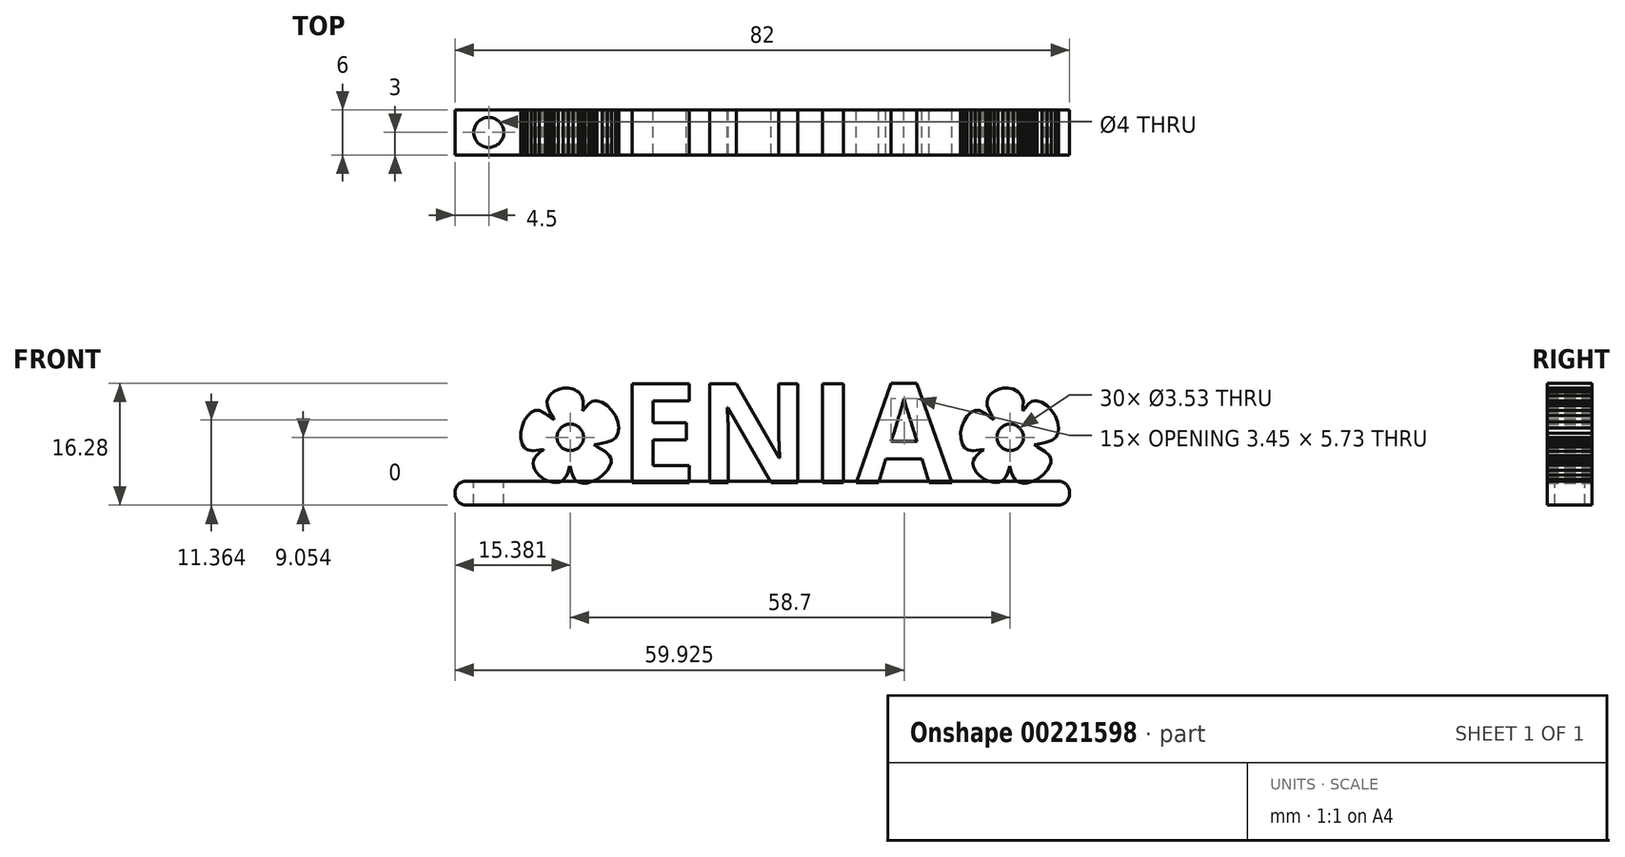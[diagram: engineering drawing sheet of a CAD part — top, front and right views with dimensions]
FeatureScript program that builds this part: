
annotation { "Feature Type Name" : "Feature", "Feature Type Description" : "" }
export const myFeature = defineFeature(function(context is Context, id is Id, definition is map)
    precondition{}
    {
        {
            var Q0;
            Q0=qCreatedBy(makeId("Front.planeOp"),FACE);
            var sketch = newSketch(context, id + "F0", { "sketchPlane" : qUnion([Q0])});
            skText(sketch, "E0", { "text": "   ENIA", "fontName": "OpenSans-Bold.ttf"});
            skLineSegment(sketch, "E1.0.0", {"start": v(-9.3, 0.1) * mm, "end": v(-8.53, 0.46) * mm});
            skLineSegment(sketch, "E1.0.1", {"start": v(-8.53, 0.46) * mm, "end": v(-7.79, 1.02) * mm});
            skLineSegment(sketch, "E1.0.2", {"start": v(-7.79, 1.02) * mm, "end": v(-7.18, 1.67) * mm});
            skLineSegment(sketch, "E1.0.3", {"start": v(-7.18, 1.67) * mm, "end": v(-6.78, 2.35) * mm});
            skLineSegment(sketch, "E1.0.4", {"start": v(-6.78, 2.35) * mm, "end": v(-6.68, 2.7) * mm});
            skLineSegment(sketch, "E1.0.5", {"start": v(-6.68, 2.7) * mm, "end": v(-6.67, 3.02) * mm});
            skLineSegment(sketch, "E1.0.6", {"start": v(-6.67, 3.02) * mm, "end": v(-6.73, 3.33) * mm});
            skLineSegment(sketch, "E1.0.7", {"start": v(-6.73, 3.33) * mm, "end": v(-6.89, 3.62) * mm});
            skLineSegment(sketch, "E1.0.8", {"start": v(-6.89, 3.62) * mm, "end": v(-7.48, 4.2) * mm});
            skLineSegment(sketch, "E1.0.9", {"start": v(-7.48, 4.2) * mm, "end": v(-8.5, 4.79) * mm});
            skLineSegment(sketch, "E1.0.10", {"start": v(-8.5, 4.79) * mm, "end": v(-8.93, 5.06) * mm});
            skLineSegment(sketch, "E1.0.11", {"start": v(-8.93, 5.06) * mm, "end": v(-8.42, 5.16) * mm});
            skLineSegment(sketch, "E1.0.12", {"start": v(-8.42, 5.16) * mm, "end": v(-7.31, 5.37) * mm});
            skLineSegment(sketch, "E1.0.13", {"start": v(-7.31, 5.37) * mm, "end": v(-6.55, 5.65) * mm});
            skLineSegment(sketch, "E1.0.14", {"start": v(-6.55, 5.65) * mm, "end": v(-6.05, 6.04) * mm});
            skLineSegment(sketch, "E1.0.15", {"start": v(-6.05, 6.04) * mm, "end": v(-5.76, 6.58) * mm});
            skLineSegment(sketch, "E1.0.16", {"start": v(-5.76, 6.58) * mm, "end": v(-5.64, 7.33) * mm});
            skLineSegment(sketch, "E1.0.17", {"start": v(-5.64, 7.33) * mm, "end": v(-5.78, 8.14) * mm});
            skLineSegment(sketch, "E1.0.18", {"start": v(-5.78, 8.14) * mm, "end": v(-6.1, 8.93) * mm});
            skLineSegment(sketch, "E1.0.19", {"start": v(-6.1, 8.93) * mm, "end": v(-6.6, 9.67) * mm});
            skLineSegment(sketch, "E1.0.20", {"start": v(-6.6, 9.67) * mm, "end": v(-7.2, 10.28) * mm});
            skLineSegment(sketch, "E1.0.21", {"start": v(-7.2, 10.28) * mm, "end": v(-7.86, 10.72) * mm});
            skLineSegment(sketch, "E1.0.22", {"start": v(-7.86, 10.72) * mm, "end": v(-8.55, 10.93) * mm});
            skLineSegment(sketch, "E1.0.23", {"start": v(-8.55, 10.93) * mm, "end": v(-8.88, 10.93) * mm});
            skLineSegment(sketch, "E1.0.24", {"start": v(-8.88, 10.93) * mm, "end": v(-9.2, 10.85) * mm});
            skLineSegment(sketch, "E1.0.25", {"start": v(-9.2, 10.85) * mm, "end": v(-9.65, 10.56) * mm});
            skLineSegment(sketch, "E1.0.26", {"start": v(-9.65, 10.56) * mm, "end": v(-10.14, 9.98) * mm});
            skLineSegment(sketch, "E1.0.27", {"start": v(-10.14, 9.98) * mm, "end": v(-10.45, 9.58) * mm});
            skLineSegment(sketch, "E1.0.28", {"start": v(-10.45, 9.58) * mm, "end": v(-10.4, 10.03) * mm});
            skLineSegment(sketch, "E1.0.29", {"start": v(-10.4, 10.03) * mm, "end": v(-10.4, 10.93) * mm});
            skLineSegment(sketch, "E1.0.30", {"start": v(-10.4, 10.93) * mm, "end": v(-10.6, 11.63) * mm});
            skLineSegment(sketch, "E1.0.31", {"start": v(-10.6, 11.63) * mm, "end": v(-11.04, 12.15) * mm});
            skLineSegment(sketch, "E1.0.32", {"start": v(-11.04, 12.15) * mm, "end": v(-11.71, 12.5) * mm});
            skLineSegment(sketch, "E1.0.33", {"start": v(-11.71, 12.5) * mm, "end": v(-12.4, 12.64) * mm});
            skLineSegment(sketch, "E1.0.34", {"start": v(-12.4, 12.64) * mm, "end": v(-13.07, 12.62) * mm});
            skLineSegment(sketch, "E1.0.35", {"start": v(-13.07, 12.62) * mm, "end": v(-13.7, 12.47) * mm});
            skLineSegment(sketch, "E1.0.36", {"start": v(-13.7, 12.47) * mm, "end": v(-14.26, 12.2) * mm});
            skLineSegment(sketch, "E1.0.37", {"start": v(-14.26, 12.2) * mm, "end": v(-14.72, 11.83) * mm});
            skLineSegment(sketch, "E1.0.38", {"start": v(-14.72, 11.83) * mm, "end": v(-15.05, 11.38) * mm});
            skLineSegment(sketch, "E1.0.39", {"start": v(-15.05, 11.38) * mm, "end": v(-15.22, 10.87) * mm});
            skLineSegment(sketch, "E1.0.40", {"start": v(-15.22, 10.87) * mm, "end": v(-15.2, 10.3) * mm});
            skLineSegment(sketch, "E1.0.41", {"start": v(-15.2, 10.3) * mm, "end": v(-14.83, 9.4) * mm});
            skLineSegment(sketch, "E1.0.42", {"start": v(-14.83, 9.4) * mm, "end": v(-14.35, 8.55) * mm});
            skLineSegment(sketch, "E1.0.43", {"start": v(-14.35, 8.55) * mm, "end": v(-14.3, 8.4) * mm});
            skLineSegment(sketch, "E1.0.44", {"start": v(-14.3, 8.4) * mm, "end": v(-14.48, 8.53) * mm});
            skLineSegment(sketch, "E1.0.45", {"start": v(-14.48, 8.53) * mm, "end": v(-15.4, 9.23) * mm});
            skLineSegment(sketch, "E1.0.46", {"start": v(-15.4, 9.23) * mm, "end": v(-16.22, 9.63) * mm});
            skLineSegment(sketch, "E1.0.47", {"start": v(-16.22, 9.63) * mm, "end": v(-16.8, 9.63) * mm});
            skLineSegment(sketch, "E1.0.48", {"start": v(-16.8, 9.63) * mm, "end": v(-17.36, 9.37) * mm});
            skLineSegment(sketch, "E1.0.49", {"start": v(-17.36, 9.37) * mm, "end": v(-17.85, 8.9) * mm});
            skLineSegment(sketch, "E1.0.50", {"start": v(-17.85, 8.9) * mm, "end": v(-18.26, 8.26) * mm});
            skLineSegment(sketch, "E1.0.51", {"start": v(-18.26, 8.26) * mm, "end": v(-18.56, 7.51) * mm});
            skLineSegment(sketch, "E1.0.52", {"start": v(-18.56, 7.51) * mm, "end": v(-18.72, 6.71) * mm});
            skLineSegment(sketch, "E1.0.53", {"start": v(-18.72, 6.71) * mm, "end": v(-18.72, 5.9) * mm});
            skLineSegment(sketch, "E1.0.54", {"start": v(-18.72, 5.9) * mm, "end": v(-18.52, 5.16) * mm});
            skLineSegment(sketch, "E1.0.55", {"start": v(-18.52, 5.16) * mm, "end": v(-18.2, 4.64) * mm});
            skLineSegment(sketch, "E1.0.56", {"start": v(-18.2, 4.64) * mm, "end": v(-17.75, 4.36) * mm});
            skLineSegment(sketch, "E1.0.57", {"start": v(-17.75, 4.36) * mm, "end": v(-17.1, 4.27) * mm});
            skLineSegment(sketch, "E1.0.58", {"start": v(-17.1, 4.27) * mm, "end": v(-16.21, 4.37) * mm});
            skLineSegment(sketch, "E1.0.59", {"start": v(-16.21, 4.37) * mm, "end": v(-15.7, 4.43) * mm});
            skLineSegment(sketch, "E1.0.60", {"start": v(-15.7, 4.43) * mm, "end": v(-15.67, 4.4) * mm});
            skLineSegment(sketch, "E1.0.61", {"start": v(-15.67, 4.4) * mm, "end": v(-15.78, 4.33) * mm});
            skLineSegment(sketch, "E1.0.62", {"start": v(-15.78, 4.33) * mm, "end": v(-16.17, 4.07) * mm});
            skLineSegment(sketch, "E1.0.63", {"start": v(-16.17, 4.07) * mm, "end": v(-16.55, 3.71) * mm});
            skLineSegment(sketch, "E1.0.64", {"start": v(-16.55, 3.71) * mm, "end": v(-16.87, 3.33) * mm});
            skLineSegment(sketch, "E1.0.65", {"start": v(-16.87, 3.33) * mm, "end": v(-17.04, 3) * mm});
            skLineSegment(sketch, "E1.0.66", {"start": v(-17.04, 3) * mm, "end": v(-17.08, 2.6) * mm});
            skLineSegment(sketch, "E1.0.67", {"start": v(-17.08, 2.6) * mm, "end": v(-17.02, 2.2) * mm});
            skLineSegment(sketch, "E1.0.68", {"start": v(-17.02, 2.2) * mm, "end": v(-16.87, 1.78) * mm});
            skLineSegment(sketch, "E1.0.69", {"start": v(-16.87, 1.78) * mm, "end": v(-16.62, 1.39) * mm});
            skLineSegment(sketch, "E1.0.70", {"start": v(-16.62, 1.39) * mm, "end": v(-16.3, 1.02) * mm});
            skLineSegment(sketch, "E1.0.71", {"start": v(-16.3, 1.02) * mm, "end": v(-15.9, 0.69) * mm});
            skLineSegment(sketch, "E1.0.72", {"start": v(-15.9, 0.69) * mm, "end": v(-15.45, 0.4) * mm});
            skLineSegment(sketch, "E1.0.73", {"start": v(-15.45, 0.4) * mm, "end": v(-14.95, 0.2) * mm});
            skLineSegment(sketch, "E1.0.74", {"start": v(-14.95, 0.2) * mm, "end": v(-14.44, 0.06) * mm});
            skLineSegment(sketch, "E1.0.75", {"start": v(-14.44, 0.06) * mm, "end": v(-13.98, 0.02) * mm});
            skLineSegment(sketch, "E1.0.76", {"start": v(-13.98, 0.02) * mm, "end": v(-13.58, 0.08) * mm});
            skLineSegment(sketch, "E1.0.77", {"start": v(-13.58, 0.08) * mm, "end": v(-13.23, 0.23) * mm});
            skLineSegment(sketch, "E1.0.78", {"start": v(-13.23, 0.23) * mm, "end": v(-12.92, 0.49) * mm});
            skLineSegment(sketch, "E1.0.79", {"start": v(-12.92, 0.49) * mm, "end": v(-12.67, 0.84) * mm});
            skLineSegment(sketch, "E1.0.80", {"start": v(-12.67, 0.84) * mm, "end": v(-12.46, 1.28) * mm});
            skLineSegment(sketch, "E1.0.81", {"start": v(-12.46, 1.28) * mm, "end": v(-12.3, 1.83) * mm});
            skLineSegment(sketch, "E1.0.82", {"start": v(-12.3, 1.83) * mm, "end": v(-12.19, 2.26) * mm});
            skLineSegment(sketch, "E1.0.83", {"start": v(-12.19, 2.26) * mm, "end": v(-12.13, 2.1) * mm});
            skLineSegment(sketch, "E1.0.84", {"start": v(-12.13, 2.1) * mm, "end": v(-12.01, 1.53) * mm});
            skLineSegment(sketch, "E1.0.85", {"start": v(-12.01, 1.53) * mm, "end": v(-11.82, 1) * mm});
            skLineSegment(sketch, "E1.0.86", {"start": v(-11.82, 1) * mm, "end": v(-11.6, 0.55) * mm});
            skLineSegment(sketch, "E1.0.87", {"start": v(-11.6, 0.55) * mm, "end": v(-11.35, 0.26) * mm});
            skLineSegment(sketch, "E1.0.88", {"start": v(-11.35, 0.26) * mm, "end": v(-10.95, 0.05) * mm});
            skLineSegment(sketch, "E1.0.89", {"start": v(-10.95, 0.05) * mm, "end": v(-10.46, -0.04) * mm});
            skLineSegment(sketch, "E1.0.90", {"start": v(-10.46, -0.04) * mm, "end": v(-9.9, -0.03) * mm});
            skLineSegment(sketch, "E1.0.91", {"start": v(-9.9, -0.03) * mm, "end": v(-9.3, 0.1) * mm});
            skCircle(sketch, "E2", {"center": v(-12.12, 6.05) * mm, "radius": 1.77 * mm});
            skCircle(sketch, "E3.1.0.0", {"center": v(46.58, 6.05) * mm, "radius": 1.77 * mm});
            skLineSegment(sketch, "E3.1.0.1", {"start": v(48.25, 9.58) * mm, "end": v(48.3, 10.03) * mm});
            skLineSegment(sketch, "E3.1.0.2", {"start": v(51.5, 10.28) * mm, "end": v(50.84, 10.72) * mm});
            skLineSegment(sketch, "E3.1.0.3", {"start": v(39.98, 5.9) * mm, "end": v(40.18, 5.16) * mm});
            skLineSegment(sketch, "E3.1.0.4", {"start": v(44.44, 12.2) * mm, "end": v(43.98, 11.83) * mm});
            skLineSegment(sketch, "E3.1.0.5", {"start": v(42.4, 1.02) * mm, "end": v(42.8, 0.69) * mm});
            skLineSegment(sketch, "E3.1.0.6", {"start": v(42.48, 9.63) * mm, "end": v(41.9, 9.63) * mm});
            skLineSegment(sketch, "E3.1.0.7", {"start": v(40.14, 7.51) * mm, "end": v(39.98, 6.71) * mm});
            skLineSegment(sketch, "E3.1.0.8", {"start": v(43.3, 9.23) * mm, "end": v(42.48, 9.63) * mm});
            skLineSegment(sketch, "E3.1.0.9", {"start": v(41.9, 9.63) * mm, "end": v(41.34, 9.37) * mm});
            skLineSegment(sketch, "E3.1.0.10", {"start": v(48.56, 9.98) * mm, "end": v(48.25, 9.58) * mm});
            skLineSegment(sketch, "E3.1.0.11", {"start": v(48.1, 11.63) * mm, "end": v(47.66, 12.15) * mm});
            skLineSegment(sketch, "E3.1.0.12", {"start": v(47.66, 12.15) * mm, "end": v(46.99, 12.5) * mm});
            skLineSegment(sketch, "E3.1.0.13", {"start": v(48.3, 10.93) * mm, "end": v(48.1, 11.63) * mm});
            skLineSegment(sketch, "E3.1.0.14", {"start": v(43.25, 0.4) * mm, "end": v(43.75, 0.2) * mm});
            skLineSegment(sketch, "E3.1.0.15", {"start": v(48.8, -0.03) * mm, "end": v(49.4, 0.1) * mm});
            skLineSegment(sketch, "E3.1.0.16", {"start": v(39.98, 6.71) * mm, "end": v(39.98, 5.9) * mm});
            skLineSegment(sketch, "E3.1.0.17", {"start": v(49.4, 0.1) * mm, "end": v(50.17, 0.46) * mm});
            skLineSegment(sketch, "E3.1.0.18", {"start": v(42.8, 0.69) * mm, "end": v(43.25, 0.4) * mm});
            skLineSegment(sketch, "E3.1.0.19", {"start": v(40.18, 5.16) * mm, "end": v(40.5, 4.64) * mm});
            skLineSegment(sketch, "E3.1.0.20", {"start": v(51.39, 5.37) * mm, "end": v(52.15, 5.65) * mm});
            skLineSegment(sketch, "E3.1.0.21", {"start": v(50.17, 0.46) * mm, "end": v(50.91, 1.02) * mm});
            skLineSegment(sketch, "E3.1.0.22", {"start": v(52.1, 9.67) * mm, "end": v(51.5, 10.28) * mm});
            skLineSegment(sketch, "E3.1.0.23", {"start": v(48.3, 10.03) * mm, "end": v(48.3, 10.93) * mm});
            skLineSegment(sketch, "E3.1.0.24", {"start": v(41.34, 9.37) * mm, "end": v(40.85, 8.9) * mm});
            skLineSegment(sketch, "E3.1.0.25", {"start": v(46.99, 12.5) * mm, "end": v(46.3, 12.64) * mm});
            skLineSegment(sketch, "E3.1.0.26", {"start": v(45.63, 12.62) * mm, "end": v(45, 12.47) * mm});
            skLineSegment(sketch, "E3.1.0.27", {"start": v(51.52, 1.67) * mm, "end": v(51.92, 2.35) * mm});
            skLineSegment(sketch, "E3.1.0.28", {"start": v(52.6, 8.93) * mm, "end": v(52.1, 9.67) * mm});
            skLineSegment(sketch, "E3.1.0.29", {"start": v(46.3, 12.64) * mm, "end": v(45.63, 12.62) * mm});
            skLineSegment(sketch, "E3.1.0.30", {"start": v(50.91, 1.02) * mm, "end": v(51.52, 1.67) * mm});
            skLineSegment(sketch, "E3.1.0.31", {"start": v(40.85, 8.9) * mm, "end": v(40.44, 8.26) * mm});
            skLineSegment(sketch, "E3.1.0.32", {"start": v(40.44, 8.26) * mm, "end": v(40.14, 7.51) * mm});
            skLineSegment(sketch, "E3.1.0.33", {"start": v(45, 12.47) * mm, "end": v(44.44, 12.2) * mm});
            skLineSegment(sketch, "E3.1.0.34", {"start": v(51.92, 2.35) * mm, "end": v(52.02, 2.7) * mm});
            skLineSegment(sketch, "E3.1.0.35", {"start": v(41.9, 9.63) * mm, "end": v(41.34, 9.37) * mm});
            skLineSegment(sketch, "E3.1.0.36", {"start": v(46.3, 12.64) * mm, "end": v(45.63, 12.62) * mm});
            skLineSegment(sketch, "E3.1.0.37", {"start": v(51.39, 5.37) * mm, "end": v(52.15, 5.65) * mm});
            skLineSegment(sketch, "E3.1.0.38", {"start": v(47.75, 0.05) * mm, "end": v(48.24, -0.04) * mm});
            skLineSegment(sketch, "E3.1.0.39", {"start": v(52.6, 8.93) * mm, "end": v(52.1, 9.67) * mm});
            skLineSegment(sketch, "E3.1.0.40", {"start": v(48.8, -0.03) * mm, "end": v(49.4, 0.1) * mm});
            skLineSegment(sketch, "E3.1.0.41", {"start": v(48.56, 9.98) * mm, "end": v(48.25, 9.58) * mm});
            skLineSegment(sketch, "E3.1.0.42", {"start": v(50.91, 1.02) * mm, "end": v(51.52, 1.67) * mm});
            skLineSegment(sketch, "E3.1.0.43", {"start": v(51.92, 2.35) * mm, "end": v(52.02, 2.7) * mm});
            skLineSegment(sketch, "E3.1.0.44", {"start": v(39.98, 6.71) * mm, "end": v(39.98, 5.9) * mm});
            skLineSegment(sketch, "E3.1.0.45", {"start": v(49.4, 0.1) * mm, "end": v(50.17, 0.46) * mm});
            skLineSegment(sketch, "E3.1.0.46", {"start": v(45.63, 12.62) * mm, "end": v(45, 12.47) * mm});
            skLineSegment(sketch, "E3.1.0.47", {"start": v(44.44, 12.2) * mm, "end": v(43.98, 11.83) * mm});
            skLineSegment(sketch, "E3.1.0.48", {"start": v(43.25, 0.4) * mm, "end": v(43.75, 0.2) * mm});
            skLineSegment(sketch, "E3.1.0.49", {"start": v(48.3, 10.03) * mm, "end": v(48.3, 10.93) * mm});
            skLineSegment(sketch, "E3.1.0.50", {"start": v(48.25, 9.58) * mm, "end": v(48.3, 10.03) * mm});
            skLineSegment(sketch, "E3.1.0.51", {"start": v(48.24, -0.04) * mm, "end": v(48.8, -0.03) * mm});
            skLineSegment(sketch, "E3.1.0.52", {"start": v(42.48, 9.63) * mm, "end": v(41.9, 9.63) * mm});
            skLineSegment(sketch, "E3.1.0.53", {"start": v(48.3, 10.93) * mm, "end": v(48.1, 11.63) * mm});
            skLineSegment(sketch, "E3.1.0.54", {"start": v(51.5, 10.28) * mm, "end": v(50.84, 10.72) * mm});
            skLineSegment(sketch, "E3.1.0.55", {"start": v(40.85, 8.9) * mm, "end": v(40.44, 8.26) * mm});
            skLineSegment(sketch, "E3.1.0.56", {"start": v(42.8, 0.69) * mm, "end": v(43.25, 0.4) * mm});
            skLineSegment(sketch, "E3.1.0.57", {"start": v(46.99, 12.5) * mm, "end": v(46.3, 12.64) * mm});
            skLineSegment(sketch, "E3.1.0.58", {"start": v(41.34, 9.37) * mm, "end": v(40.85, 8.9) * mm});
            skLineSegment(sketch, "E3.1.0.59", {"start": v(39.98, 5.9) * mm, "end": v(40.18, 5.16) * mm});
            skLineSegment(sketch, "E3.1.0.60", {"start": v(47.66, 12.15) * mm, "end": v(46.99, 12.5) * mm});
            skLineSegment(sketch, "E3.1.0.61", {"start": v(43.3, 9.23) * mm, "end": v(42.48, 9.63) * mm});
            skLineSegment(sketch, "E3.1.0.62", {"start": v(50.17, 0.46) * mm, "end": v(50.91, 1.02) * mm});
            skLineSegment(sketch, "E3.1.0.63", {"start": v(48.1, 11.63) * mm, "end": v(47.66, 12.15) * mm});
            skLineSegment(sketch, "E3.1.0.64", {"start": v(40.44, 8.26) * mm, "end": v(40.14, 7.51) * mm});
            skLineSegment(sketch, "E3.1.0.65", {"start": v(51.52, 1.67) * mm, "end": v(51.92, 2.35) * mm});
            skLineSegment(sketch, "E3.1.0.66", {"start": v(40.14, 7.51) * mm, "end": v(39.98, 6.71) * mm});
            skLineSegment(sketch, "E3.1.0.67", {"start": v(42.4, 1.02) * mm, "end": v(42.8, 0.69) * mm});
            skLineSegment(sketch, "E3.1.0.68", {"start": v(40.18, 5.16) * mm, "end": v(40.5, 4.64) * mm});
            skLineSegment(sketch, "E3.1.0.69", {"start": v(45, 12.47) * mm, "end": v(44.44, 12.2) * mm});
            skLineSegment(sketch, "E3.1.0.70", {"start": v(52.1, 9.67) * mm, "end": v(51.5, 10.28) * mm});
            skLineSegment(sketch, "E3.1.0.71", {"start": v(43.98, 11.83) * mm, "end": v(43.65, 11.38) * mm});
            skLineSegment(sketch, "E3.1.0.72", {"start": v(50.84, 10.72) * mm, "end": v(50.15, 10.93) * mm});
            skLineSegment(sketch, "E3.1.0.73", {"start": v(52.65, 6.04) * mm, "end": v(52.94, 6.58) * mm});
            skLineSegment(sketch, "E3.1.0.74", {"start": v(52.02, 2.7) * mm, "end": v(52.03, 3.02) * mm});
            skLineSegment(sketch, "E3.1.0.75", {"start": v(50.15, 10.93) * mm, "end": v(49.82, 10.93) * mm});
            skLineSegment(sketch, "E3.1.0.76", {"start": v(40.5, 4.64) * mm, "end": v(40.95, 4.36) * mm});
            skLineSegment(sketch, "E3.1.0.77", {"start": v(49.5, 10.85) * mm, "end": v(49.05, 10.56) * mm});
            skLineSegment(sketch, "E3.1.0.78", {"start": v(50.28, 5.16) * mm, "end": v(51.39, 5.37) * mm});
            skLineSegment(sketch, "E3.1.0.79", {"start": v(52.03, 3.02) * mm, "end": v(51.97, 3.33) * mm});
            skLineSegment(sketch, "E3.1.0.80", {"start": v(51.97, 3.33) * mm, "end": v(51.81, 3.62) * mm});
            skLineSegment(sketch, "E3.1.0.81", {"start": v(51.22, 4.2) * mm, "end": v(50.2, 4.79) * mm});
            skLineSegment(sketch, "E3.1.0.82", {"start": v(53.06, 7.33) * mm, "end": v(52.92, 8.14) * mm});
            skLineSegment(sketch, "E3.1.0.83", {"start": v(42.08, 1.39) * mm, "end": v(42.4, 1.02) * mm});
            skLineSegment(sketch, "E3.1.0.84", {"start": v(44.26, 0.06) * mm, "end": v(44.72, 0.02) * mm});
            skLineSegment(sketch, "E3.1.0.85", {"start": v(49.77, 5.06) * mm, "end": v(50.28, 5.16) * mm});
            skLineSegment(sketch, "E3.1.0.86", {"start": v(47.35, 0.26) * mm, "end": v(47.75, 0.05) * mm});
            skLineSegment(sketch, "E3.1.0.87", {"start": v(43.65, 11.38) * mm, "end": v(43.48, 10.87) * mm});
            skLineSegment(sketch, "E3.1.0.88", {"start": v(52.94, 6.58) * mm, "end": v(53.06, 7.33) * mm});
            skLineSegment(sketch, "E3.1.0.89", {"start": v(47.75, 0.05) * mm, "end": v(48.24, -0.04) * mm});
            skLineSegment(sketch, "E3.1.0.90", {"start": v(50.2, 4.79) * mm, "end": v(49.77, 5.06) * mm});
            skLineSegment(sketch, "E3.1.0.91", {"start": v(43.75, 0.2) * mm, "end": v(44.26, 0.06) * mm});
            skLineSegment(sketch, "E3.1.0.92", {"start": v(43.5, 10.3) * mm, "end": v(43.87, 9.4) * mm});
            skLineSegment(sketch, "E3.1.0.93", {"start": v(41.83, 1.78) * mm, "end": v(42.08, 1.39) * mm});
            skLineSegment(sketch, "E3.1.0.94", {"start": v(51.81, 3.62) * mm, "end": v(51.22, 4.2) * mm});
            skLineSegment(sketch, "E3.1.0.95", {"start": v(48.24, -0.04) * mm, "end": v(48.8, -0.03) * mm});
            skLineSegment(sketch, "E3.1.0.96", {"start": v(43.48, 10.87) * mm, "end": v(43.5, 10.3) * mm});
            skLineSegment(sketch, "E3.1.0.97", {"start": v(52.15, 5.65) * mm, "end": v(52.65, 6.04) * mm});
            skLineSegment(sketch, "E3.1.0.98", {"start": v(49.82, 10.93) * mm, "end": v(49.5, 10.85) * mm});
            skLineSegment(sketch, "E3.1.0.99", {"start": v(49.05, 10.56) * mm, "end": v(48.56, 9.98) * mm});
            skLineSegment(sketch, "E3.1.0.100", {"start": v(44.72, 0.02) * mm, "end": v(45.12, 0.08) * mm});
            skLineSegment(sketch, "E3.1.0.101", {"start": v(41.68, 2.2) * mm, "end": v(41.83, 1.78) * mm});
            skLineSegment(sketch, "E3.1.0.102", {"start": v(52.92, 8.14) * mm, "end": v(52.6, 8.93) * mm});
            skLineSegment(sketch, "E3.1.0.103", {"start": v(50.2, 4.79) * mm, "end": v(49.77, 5.06) * mm});
            skLineSegment(sketch, "E3.1.0.104", {"start": v(49.77, 5.06) * mm, "end": v(50.28, 5.16) * mm});
            skLineSegment(sketch, "E3.1.0.105", {"start": v(40.5, 4.64) * mm, "end": v(40.95, 4.36) * mm});
            skLineSegment(sketch, "E3.1.0.106", {"start": v(47.1, 0.55) * mm, "end": v(47.35, 0.26) * mm});
            skLineSegment(sketch, "E3.1.0.107", {"start": v(47.35, 0.26) * mm, "end": v(47.75, 0.05) * mm});
            skLineSegment(sketch, "E3.1.0.108", {"start": v(41.83, 1.78) * mm, "end": v(42.08, 1.39) * mm});
            skLineSegment(sketch, "E3.1.0.109", {"start": v(51.81, 3.62) * mm, "end": v(51.22, 4.2) * mm});
            skLineSegment(sketch, "E3.1.0.110", {"start": v(50.28, 5.16) * mm, "end": v(51.39, 5.37) * mm});
            skLineSegment(sketch, "E3.1.0.111", {"start": v(43.5, 10.3) * mm, "end": v(43.87, 9.4) * mm});
            skLineSegment(sketch, "E3.1.0.112", {"start": v(52.15, 5.65) * mm, "end": v(52.65, 6.04) * mm});
            skLineSegment(sketch, "E3.1.0.113", {"start": v(49.05, 10.56) * mm, "end": v(48.56, 9.98) * mm});
            skLineSegment(sketch, "E3.1.0.114", {"start": v(52.94, 6.58) * mm, "end": v(53.06, 7.33) * mm});
            skLineSegment(sketch, "E3.1.0.115", {"start": v(43.48, 10.87) * mm, "end": v(43.5, 10.3) * mm});
            skLineSegment(sketch, "E3.1.0.116", {"start": v(49.82, 10.93) * mm, "end": v(49.5, 10.85) * mm});
            skLineSegment(sketch, "E3.1.0.117", {"start": v(44.72, 0.02) * mm, "end": v(45.12, 0.08) * mm});
            skLineSegment(sketch, "E3.1.0.118", {"start": v(49.5, 10.85) * mm, "end": v(49.05, 10.56) * mm});
            skLineSegment(sketch, "E3.1.0.119", {"start": v(44.26, 0.06) * mm, "end": v(44.72, 0.02) * mm});
            skLineSegment(sketch, "E3.1.0.120", {"start": v(43.75, 0.2) * mm, "end": v(44.26, 0.06) * mm});
            skLineSegment(sketch, "E3.1.0.121", {"start": v(51.22, 4.2) * mm, "end": v(50.2, 4.79) * mm});
            skLineSegment(sketch, "E3.1.0.122", {"start": v(52.65, 6.04) * mm, "end": v(52.94, 6.58) * mm});
            skLineSegment(sketch, "E3.1.0.123", {"start": v(41.62, 2.6) * mm, "end": v(41.68, 2.2) * mm});
            skLineSegment(sketch, "E3.1.0.124", {"start": v(52.02, 2.7) * mm, "end": v(52.03, 3.02) * mm});
            skLineSegment(sketch, "E3.1.0.125", {"start": v(42.08, 1.39) * mm, "end": v(42.4, 1.02) * mm});
            skLineSegment(sketch, "E3.1.0.126", {"start": v(52.92, 8.14) * mm, "end": v(52.6, 8.93) * mm});
            skLineSegment(sketch, "E3.1.0.127", {"start": v(53.06, 7.33) * mm, "end": v(52.92, 8.14) * mm});
            skLineSegment(sketch, "E3.1.0.128", {"start": v(52.03, 3.02) * mm, "end": v(51.97, 3.33) * mm});
            skLineSegment(sketch, "E3.1.0.129", {"start": v(41.68, 2.2) * mm, "end": v(41.83, 1.78) * mm});
            skLineSegment(sketch, "E3.1.0.130", {"start": v(51.97, 3.33) * mm, "end": v(51.81, 3.62) * mm});
            skLineSegment(sketch, "E3.1.0.131", {"start": v(43.65, 11.38) * mm, "end": v(43.48, 10.87) * mm});
            skLineSegment(sketch, "E3.1.0.132", {"start": v(50.15, 10.93) * mm, "end": v(49.82, 10.93) * mm});
            skLineSegment(sketch, "E3.1.0.133", {"start": v(50.84, 10.72) * mm, "end": v(50.15, 10.93) * mm});
            skLineSegment(sketch, "E3.1.0.134", {"start": v(43.98, 11.83) * mm, "end": v(43.65, 11.38) * mm});
            skLineSegment(sketch, "E3.1.0.135", {"start": v(41.62, 2.6) * mm, "end": v(41.68, 2.2) * mm});
            skLineSegment(sketch, "E3.1.0.136", {"start": v(42.49, 4.37) * mm, "end": v(43, 4.43) * mm});
            skLineSegment(sketch, "E3.1.0.137", {"start": v(46.69, 1.53) * mm, "end": v(46.88, 1) * mm});
            skLineSegment(sketch, "E3.1.0.138", {"start": v(42.92, 4.33) * mm, "end": v(42.53, 4.07) * mm});
            skLineSegment(sketch, "E3.1.0.139", {"start": v(45.47, 0.23) * mm, "end": v(45.78, 0.49) * mm});
            skLineSegment(sketch, "E3.1.0.140", {"start": v(46.03, 0.84) * mm, "end": v(46.24, 1.28) * mm});
            skLineSegment(sketch, "E3.1.0.141", {"start": v(46.88, 1) * mm, "end": v(47.1, 0.55) * mm});
            skLineSegment(sketch, "E3.1.0.142", {"start": v(42.53, 4.07) * mm, "end": v(42.15, 3.71) * mm});
            skLineSegment(sketch, "E3.1.0.143", {"start": v(46.57, 2.1) * mm, "end": v(46.69, 1.53) * mm});
            skLineSegment(sketch, "E3.1.0.144", {"start": v(45.78, 0.49) * mm, "end": v(46.03, 0.84) * mm});
            skLineSegment(sketch, "E3.1.0.145", {"start": v(41.6, 4.27) * mm, "end": v(42.49, 4.37) * mm});
            skLineSegment(sketch, "E3.1.0.146", {"start": v(42.15, 3.71) * mm, "end": v(41.83, 3.33) * mm});
            skLineSegment(sketch, "E3.1.0.147", {"start": v(40.95, 4.36) * mm, "end": v(41.6, 4.27) * mm});
            skLineSegment(sketch, "E3.1.0.148", {"start": v(46.24, 1.28) * mm, "end": v(46.4, 1.83) * mm});
            skLineSegment(sketch, "E3.1.0.149", {"start": v(46.51, 2.26) * mm, "end": v(46.57, 2.1) * mm});
            skLineSegment(sketch, "E3.1.0.150", {"start": v(41.83, 3.33) * mm, "end": v(41.66, 3) * mm});
            skLineSegment(sketch, "E3.1.0.151", {"start": v(47.1, 0.55) * mm, "end": v(47.35, 0.26) * mm});
            skLineSegment(sketch, "E3.1.0.152", {"start": v(46.4, 1.83) * mm, "end": v(46.51, 2.26) * mm});
            skLineSegment(sketch, "E3.1.0.153", {"start": v(41.66, 3) * mm, "end": v(41.62, 2.6) * mm});
            skLineSegment(sketch, "E3.1.0.154", {"start": v(45.12, 0.08) * mm, "end": v(45.47, 0.23) * mm});
            skLineSegment(sketch, "E3.1.0.155", {"start": v(43.03, 4.4) * mm, "end": v(42.92, 4.33) * mm});
            skLineSegment(sketch, "E3.1.0.156", {"start": v(46.51, 2.26) * mm, "end": v(46.57, 2.1) * mm});
            skLineSegment(sketch, "E3.1.0.157", {"start": v(41.6, 4.27) * mm, "end": v(42.49, 4.37) * mm});
            skLineSegment(sketch, "E3.1.0.158", {"start": v(46.69, 1.53) * mm, "end": v(46.88, 1) * mm});
            skLineSegment(sketch, "E3.1.0.159", {"start": v(43, 4.43) * mm, "end": v(43.03, 4.4) * mm});
            skLineSegment(sketch, "E3.1.0.160", {"start": v(42.15, 3.71) * mm, "end": v(41.83, 3.33) * mm});
            skLineSegment(sketch, "E3.1.0.161", {"start": v(40.95, 4.36) * mm, "end": v(41.6, 4.27) * mm});
            skLineSegment(sketch, "E3.1.0.162", {"start": v(42.49, 4.37) * mm, "end": v(43, 4.43) * mm});
            skLineSegment(sketch, "E3.1.0.163", {"start": v(45.12, 0.08) * mm, "end": v(45.47, 0.23) * mm});
            skLineSegment(sketch, "E3.1.0.164", {"start": v(42.53, 4.07) * mm, "end": v(42.15, 3.71) * mm});
            skLineSegment(sketch, "E3.1.0.165", {"start": v(46.57, 2.1) * mm, "end": v(46.69, 1.53) * mm});
            skLineSegment(sketch, "E3.1.0.166", {"start": v(46.4, 1.83) * mm, "end": v(46.51, 2.26) * mm});
            skLineSegment(sketch, "E3.1.0.167", {"start": v(42.92, 4.33) * mm, "end": v(42.53, 4.07) * mm});
            skLineSegment(sketch, "E3.1.0.168", {"start": v(45.47, 0.23) * mm, "end": v(45.78, 0.49) * mm});
            skLineSegment(sketch, "E3.1.0.169", {"start": v(41.66, 3) * mm, "end": v(41.62, 2.6) * mm});
            skLineSegment(sketch, "E3.1.0.170", {"start": v(46.88, 1) * mm, "end": v(47.1, 0.55) * mm});
            skLineSegment(sketch, "E3.1.0.171", {"start": v(45.78, 0.49) * mm, "end": v(46.03, 0.84) * mm});
            skLineSegment(sketch, "E3.1.0.172", {"start": v(46.03, 0.84) * mm, "end": v(46.24, 1.28) * mm});
            skLineSegment(sketch, "E3.1.0.173", {"start": v(41.83, 3.33) * mm, "end": v(41.66, 3) * mm});
            skLineSegment(sketch, "E3.1.0.174", {"start": v(46.24, 1.28) * mm, "end": v(46.4, 1.83) * mm});
            skLineSegment(sketch, "E3.1.0.175", {"start": v(43.03, 4.4) * mm, "end": v(42.92, 4.33) * mm});
            skLineSegment(sketch, "E3.1.0.176", {"start": v(43, 4.43) * mm, "end": v(43.03, 4.4) * mm});
            skLineSegment(sketch, "E3.1.0.177", {"start": v(44.4, 8.4) * mm, "end": v(44.22, 8.53) * mm});
            skLineSegment(sketch, "E3.1.0.178", {"start": v(44.35, 8.55) * mm, "end": v(44.4, 8.4) * mm});
            skLineSegment(sketch, "E3.1.0.179", {"start": v(43.87, 9.4) * mm, "end": v(44.35, 8.55) * mm});
            skLineSegment(sketch, "E3.1.0.180", {"start": v(44.22, 8.53) * mm, "end": v(43.3, 9.23) * mm});
            skLineSegment(sketch, "E3.1.0.181", {"start": v(44.35, 8.55) * mm, "end": v(44.4, 8.4) * mm});
            skLineSegment(sketch, "E3.1.0.182", {"start": v(43.87, 9.4) * mm, "end": v(44.35, 8.55) * mm});
            skLineSegment(sketch, "E3.1.0.183", {"start": v(44.22, 8.53) * mm, "end": v(43.3, 9.23) * mm});
            skLineSegment(sketch, "E3.1.0.184", {"start": v(44.4, 8.4) * mm, "end": v(44.22, 8.53) * mm});
            skLineSegment(sketch, "E3.direction1", {"start": v(-16.3, 1.02) * mm, "end": v(42.4, 1.02) * mm, "construction": true});
            const initialGuessF0  = {"E0": [-0.02, 0, 1, 0, 0.01334]};
            skSetInitialGuess(sketch, initialGuessF0);
            skSolve(sketch);
        }
        {
            var Q0;
            Q0=qSketchRegion(id+"F0",true);
            extrude(context, id + "F1", {"entities" : qUnion([Q0]), "endBound" : BoundingType.SYMMETRIC, "depth" : 6 * mm});
        }
        {
            var Q0;
            Q0=qCreatedBy(makeId("Top.planeOp"),FACE);
            var sketch = newSketch(context, id + "F2", { "sketchPlane" : qUnion([Q0])});
            skLineSegment(sketch, "E4.bottom", {"start": v(-20, 3) * mm, "end": v(54.5, 3) * mm});
            skLineSegment(sketch, "E4.top", {"start": v(-20, -3) * mm, "end": v(54.5, -3) * mm});
            skLineSegment(sketch, "E4.left", {"start": v(-20, 3) * mm, "end": v(-20, -3) * mm});
            skLineSegment(sketch, "E4.right", {"start": v(54.5, 3) * mm, "end": v(54.5, -3) * mm});
            skSolve(sketch);
        }
        {
            var Q0;
            Q0=makeQuery(id+"F2.imprint","IMPRINT",FACE,{"disambiguationData":[TD([[makeQuery(id+"F2.imprint","IMPRINT",EDGE,{"derivedFrom":sQuery(id+"F2.wireOp",EDGE,"E4.bottom")}),-1.0]])]});
            extrude(context, id + "F3", {"entities" : qUnion([Q0]), "depth" : 0.2 * mm});
        }
        {
            var Q0;
            Q0=makeQuery(id+"F3.opExtrude","CAP_FACE",FACE,{"disambiguationData":[OSD([sQuery(id+"F2.wireOp",EDGE,"E4.bottom"),sQuery(id+"F2.wireOp",EDGE,"E4.top"),sQuery(id+"F2.wireOp",EDGE,"E4.left"),sQuery(id+"F2.wireOp",EDGE,"E4.right")])],"isStart":true});
            extrude(context, id + "F4", {"entities" : qUnion([Q0]), "depth" : 3 * mm});
        }
        {
            var Q0;
            {var subQ0=sQuery(id+"F2.wireOp",EDGE,"E4.left");Q0=makeQuery(id+"FaVoHrOpcFZXiYX_6.opBoolean","MERGE",FACE,{"derivedFrom":[makeQuery(id+"F3.opExtrude","SWEPT_FACE",FACE,{"disambiguationData":[OSD([subQ0])]}),makeQuery(id+"F4.opExtrude","SWEPT_FACE",FACE,{"disambiguationData":[OSD([subQ0])]})]});}
            var sketch = newSketch(context, id + "F5", { "sketchPlane" : qUnion([Q0])});
            skLineSegment(sketch, "E5.bottom", {"start": v(-3, -3) * mm, "end": v(3, -3) * mm});
            skLineSegment(sketch, "E5.top", {"start": v(-3, 0.2) * mm, "end": v(3, 0.2) * mm});
            skLineSegment(sketch, "E5.left", {"start": v(-3, -3) * mm, "end": v(-3, 0.2) * mm});
            skLineSegment(sketch, "E5.right", {"start": v(3, -3) * mm, "end": v(3, 0.2) * mm});
            skSolve(sketch);
        }
        {
            var Q0;
            Q0=qSketchRegion(id+"F5",true);
            extrude(context, id + "F6", {"entities" : qUnion([Q0]), "operationType" : NewBodyOperationType.ADD, "depth" : 7.5 * mm});
        }
        {
            var Q0;
            Q0=makeQuery(id+"F6.opExtrude","CAP_EDGE",EDGE,{"disambiguationData":[OSD([sQuery(id+"F5.wireOp",EDGE,"E5.bottom")])],"isStart":false});
            var Q1;
            Q1=makeQuery(id+"F6.opExtrude","CAP_EDGE",EDGE,{"disambiguationData":[OSD([sQuery(id+"F5.wireOp",EDGE,"E5.top")])],"isStart":false});
            var Q2;
            Q2=makeQuery(id+"F4.opExtrude","CAP_EDGE",EDGE,{"disambiguationData":[OSD([sQuery(id+"F2.wireOp",EDGE,"E4.right")])],"isStart":false});
            fillet(context, id + "F7", {"entities" : qUnion([Q0, Q1, Q2]), "radius" : 1.5 * mm, "tangentPropagation" : true, "allowEdgeOverflow" : false});
        }
        {
            var Q0;
            {var subQ19=sQuery(id+"F2.wireOp",EDGE,"E4.top");var subQ20=sQuery(id+"F2.wireOp",EDGE,"E4.bottom");var subQ63=sQuery(id+"F0.wireOp",EDGE,"E0.sketch_text.stroke-2");var subQ66=sQuery(id+"F2.wireOp",EDGE,"E4.left");Q0=makeQuery(id+"F6.boolean.opBoolean","MERGE",FACE,{"derivedFrom":[makeQuery(id+"FaVoHrOpcFZXiYX_6.opBoolean","SPLIT",FACE,{"disambiguationData":[TD([makeQuery(id+"F1.opExtrude","SWEPT_FACE",FACE,{"disambiguationData":[OSD([subQ63])]})])],"derivedFrom":makeQuery(id+"F3.opExtrude","CAP_FACE",FACE,{"disambiguationData":[OSD([subQ20,subQ19,subQ66,sQuery(id+"F2.wireOp",EDGE,"E4.right")])],"isStart":false})}),makeQuery(id+"F6.opExtrude","SWEPT_FACE",FACE,{"disambiguationData":[OSD([sQuery(id+"F5.wireOp",EDGE,"E5.top")])]})]});}
            var sketch = newSketch(context, id + "F8", { "sketchPlane" : qUnion([Q0])});
            skCircle(sketch, "E6", {"center": v(-23, 0) * mm, "radius": 2 * mm});
            skSolve(sketch);
        }
        {
            var Q0;
            Q0=makeQuery(id+"F8.imprint","IMPRINT",FACE,{"disambiguationData":[TD([[makeQuery(id+"F8.imprint","IMPRINT",EDGE,{"derivedFrom":sQuery(id+"F8.wireOp",EDGE,"E6")}),1.0]])]});
            extrude(context, id + "F9", {"entities" : qUnion([Q0]), "operationType" : NewBodyOperationType.REMOVE, "oppositeDirection" : true, "depth" : 4 * mm});
        }
        {
            var Q0;
            Q0=makeQuery(id+"F3.opExtrude","CAP_EDGE",EDGE,{"disambiguationData":[OSD([sQuery(id+"F2.wireOp",EDGE,"E4.right")])],"isStart":false});
            fillet(context, id + "F10", {"entities" : qUnion([Q0]), "radius" : 1.5 * mm, "tangentPropagation" : true, "allowEdgeOverflow" : false});
        }
    });
